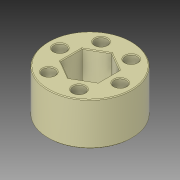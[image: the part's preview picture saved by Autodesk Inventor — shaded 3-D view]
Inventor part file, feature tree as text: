
AUTODESK INVENTOR PART (.ipt)
format: ipt  version: 2018 (Build 220112000, 112)  size: 174,080 bytes
history: native  units: in
note: dims shown in document units (in); Inventor stores cm internally (conversion verified against a paired STEP export)
features: extrude x3, chamfer x3, sketch x3, pattern_circular x1
ambient origin geometry x8: Origin, YZ Plane, XZ Plane, XY Plane, X Axis, Y Axis, Z Axis, Center Point
bodies: Solid1 (feature_tree)
feature tree (10):
  extrude  "Extrusion1"  Depth=0.57in TaperAngle=0.0deg
  extrude  "Extrusion2"  Depth=0.16in
  chamfer  "Chamfer1"  Distance=0.805in
  pattern_circular  "Circular Pattern1"  Count=6 Angle=360.0deg
  chamfer  "Chamfer2"  Distance=0.01in Angle=45.0deg
  extrude  "Extrusion3"  Depth=0.502in
  chamfer  "Chamfer3"  Distance=0.57in
  sketch  "Sketch1"  dims[d0=1.124in d1=0.57in d2=0.0in]
  sketch  "Sketch2"  dims[d3=0.81in d4=0.16in d5=0.805in d6=0.0in]
  sketch  "Sketch3"  dims[d7=0.01in d8=0.125in d9=45.0deg d10=2.3622in d11=360.0deg d13=0.01in d14=0.125in d15=45.0deg d16=0.502in d17=0.57in d18=0.0in d19=0.01in d20=0.125in d21=45.0deg]
